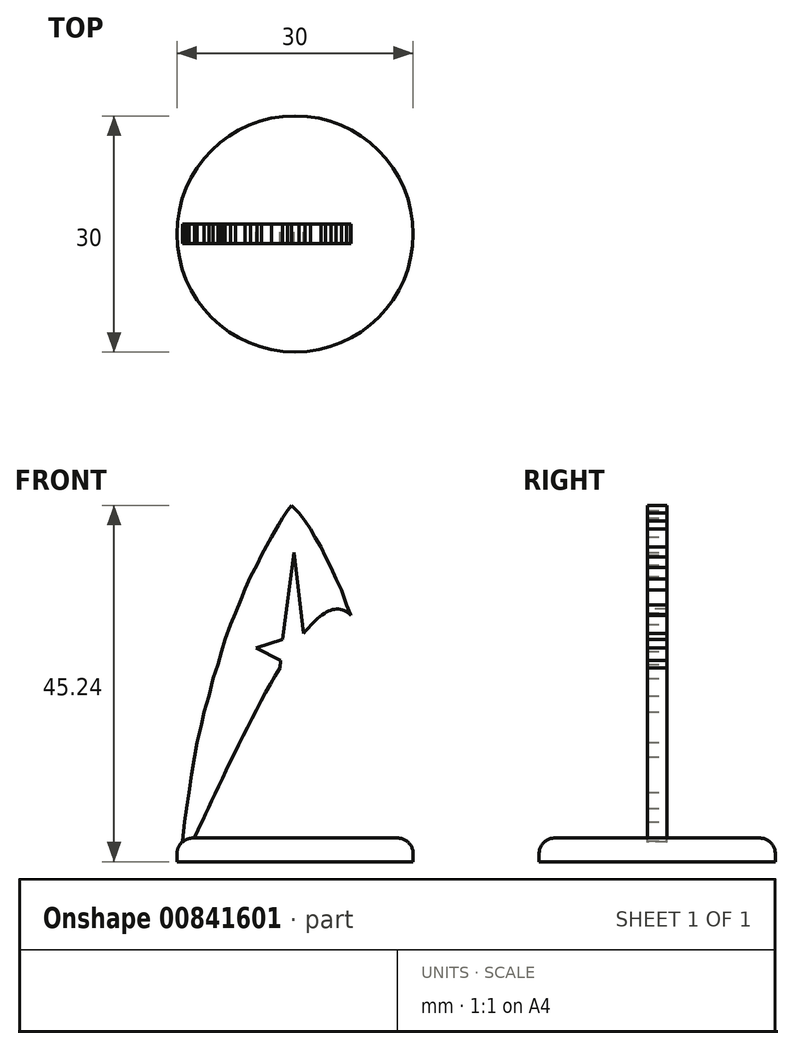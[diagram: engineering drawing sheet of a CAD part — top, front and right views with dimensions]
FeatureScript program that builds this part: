
annotation { "Feature Type Name" : "Feature", "Feature Type Description" : "" }
export const myFeature = defineFeature(function(context is Context, id is Id, definition is map)
    precondition{}
    {
        {
            var Q0;
            Q0=qCreatedBy(makeId("Top.planeOp"),FACE);
            var sketch = newSketch(context, id + "F0", { "sketchPlane" : qUnion([Q0])});
            skCircle(sketch, "E0", {"center": v(0, 0) * mm, "radius": 15 * mm});
            skSolve(sketch);
        }
        {
            var Q0;
            Q0=makeQuery(id+"F0.imprint","IMPRINT",FACE,{"disambiguationData":[TD([[makeQuery(id+"F0.imprint","IMPRINT",EDGE,{"derivedFrom":sQuery(id+"F0.wireOp",EDGE,"E0")}),1.0]])]});
            extrude(context, id + "F1", {"entities" : qUnion([Q0]), "depth" : 3 * mm, "offsetDistance" : 25 * mm});
        }
        {
            var Q0;
            Q0=makeQuery(id+"F1.opExtrude","CAP_EDGE",EDGE,{"disambiguationData":[OSD([sQuery(id+"F0.wireOp",EDGE,"E0")])],"isStart":false});
            fillet(context, id + "F2", {"entities" : qUnion([Q0]), "radius" : 2 * mm, "tangentPropagation" : true, "allowEdgeOverflow" : false});
        }
        {
            var Q0;
            Q0=qCreatedBy(makeId("Front.planeOp"),FACE);
            var sketch = newSketch(context, id + "F3", { "sketchPlane" : qUnion([Q0])});
            skLineSegment(sketch, "E1", {"start": v(-2.26, 21.82) * mm, "end": v(-1.82, 25.53) * mm});
            skLineSegment(sketch, "E2", {"start": v(-1.82, 25.53) * mm, "end": v(-4.93, 27.14) * mm});
            skLineSegment(sketch, "E3", {"start": v(-4.93, 27.14) * mm, "end": v(-1.58, 28.23) * mm});
            skLineSegment(sketch, "E4", {"start": v(-1.58, 28.23) * mm, "end": v(-0.16, 39.29) * mm});
            skLineSegment(sketch, "E5", {"start": v(-0.16, 39.29) * mm, "end": v(1.18, 28.23) * mm});
            skLineSegment(sketch, "E6", {"start": v(1.18, 28.23) * mm, "end": v(4.54, 27.08) * mm});
            skLineSegment(sketch, "E7", {"start": v(4.54, 27.08) * mm, "end": v(1.53, 25.49) * mm});
            skLineSegment(sketch, "E8", {"start": v(1.53, 25.49) * mm, "end": v(1.92, 21.96) * mm});
            skLineSegment(sketch, "E9", {"start": v(1.92, 21.96) * mm, "end": v(-0.11, 25.36) * mm});
            skLineSegment(sketch, "E10", {"start": v(-0.11, 25.36) * mm, "end": v(-2.26, 21.82) * mm});
            skLineSegment(sketch, "E11", {"start": v(-14.46, 0) * mm, "end": v(-14.28, 2.65) * mm});
            skLineSegment(sketch, "E12", {"start": v(-14.28, 2.65) * mm, "end": v(-14.02, 5.03) * mm});
            skLineSegment(sketch, "E13", {"start": v(-14.02, 5.03) * mm, "end": v(-13.75, 6.8) * mm});
            skLineSegment(sketch, "E14", {"start": v(-13.75, 6.8) * mm, "end": v(-13.49, 8.82) * mm});
            skLineSegment(sketch, "E15", {"start": v(-13.49, 8.82) * mm, "end": v(-13.14, 11.11) * mm});
            skLineSegment(sketch, "E16", {"start": v(-13.14, 11.11) * mm, "end": v(-12.78, 13.32) * mm});
            skLineSegment(sketch, "E17", {"start": v(-12.78, 13.32) * mm, "end": v(-12.43, 15.17) * mm});
            skLineSegment(sketch, "E18", {"start": v(-12.43, 15.17) * mm, "end": v(-11.9, 17.46) * mm});
            skLineSegment(sketch, "E19", {"start": v(-11.9, 17.46) * mm, "end": v(-11.55, 19.05) * mm});
            skLineSegment(sketch, "E20", {"start": v(-11.55, 19.05) * mm, "end": v(-10.93, 21.08) * mm});
            skLineSegment(sketch, "E21", {"start": v(-10.93, 21.08) * mm, "end": v(-10.4, 23.28) * mm});
            skLineSegment(sketch, "E22", {"start": v(-10.4, 23.28) * mm, "end": v(-9.78, 25.05) * mm});
            skLineSegment(sketch, "E23", {"start": v(-9.78, 25.05) * mm, "end": v(-9.34, 26.72) * mm});
            skLineSegment(sketch, "E24", {"start": v(-9.34, 26.72) * mm, "end": v(-8.9, 28.22) * mm});
            skLineSegment(sketch, "E25", {"start": v(-8.9, 28.22) * mm, "end": v(-8.2, 30.16) * mm});
            skLineSegment(sketch, "E26", {"start": v(-8.2, 30.16) * mm, "end": v(-7.58, 31.57) * mm});
            skLineSegment(sketch, "E27", {"start": v(-7.58, 31.57) * mm, "end": v(-6.87, 33.34) * mm});
            skLineSegment(sketch, "E28", {"start": v(-6.87, 33.34) * mm, "end": v(-6.34, 34.66) * mm});
            skLineSegment(sketch, "E29", {"start": v(-6.34, 34.66) * mm, "end": v(-5.64, 36.25) * mm});
            skLineSegment(sketch, "E30", {"start": v(-5.64, 36.25) * mm, "end": v(-4.85, 37.66) * mm});
            skLineSegment(sketch, "E31", {"start": v(-4.85, 37.66) * mm, "end": v(-4.23, 38.98) * mm});
            skLineSegment(sketch, "E32", {"start": v(-4.23, 38.98) * mm, "end": v(-3.61, 40.13) * mm});
            skLineSegment(sketch, "E33", {"start": v(-3.61, 40.13) * mm, "end": v(-3, 41.28) * mm});
            skLineSegment(sketch, "E34", {"start": v(-3, 41.28) * mm, "end": v(-2.11, 42.77) * mm});
            skLineSegment(sketch, "E35", {"start": v(-2.11, 42.77) * mm, "end": v(-1.58, 43.66) * mm});
            skLineSegment(sketch, "E36", {"start": v(-1.58, 43.66) * mm, "end": v(-0.96, 44.63) * mm});
            skLineSegment(sketch, "E37", {"start": v(-0.96, 44.63) * mm, "end": v(-0.44, 45.24) * mm});
            skLineSegment(sketch, "E38", {"start": v(-0.44, 45.24) * mm, "end": v(0.53, 44.27) * mm});
            skLineSegment(sketch, "E39", {"start": v(0.53, 44.27) * mm, "end": v(1.24, 43.3) * mm});
            skLineSegment(sketch, "E40", {"start": v(1.24, 43.3) * mm, "end": v(1.95, 42.25) * mm});
            skLineSegment(sketch, "E41", {"start": v(1.95, 42.25) * mm, "end": v(2.56, 41.19) * mm});
            skLineSegment(sketch, "E42", {"start": v(2.56, 41.19) * mm, "end": v(3.27, 39.95) * mm});
            skLineSegment(sketch, "E43", {"start": v(3.27, 39.95) * mm, "end": v(3.89, 38.72) * mm});
            skLineSegment(sketch, "E44", {"start": v(3.89, 38.72) * mm, "end": v(4.6, 37.4) * mm});
            skLineSegment(sketch, "E45", {"start": v(4.6, 37.4) * mm, "end": v(5.2, 35.9) * mm});
            skLineSegment(sketch, "E46", {"start": v(5.2, 35.9) * mm, "end": v(5.91, 34.48) * mm});
            skLineSegment(sketch, "E47", {"start": v(5.91, 34.48) * mm, "end": v(6.53, 32.63) * mm});
            skLineSegment(sketch, "E48", {"start": v(6.53, 32.63) * mm, "end": v(7.06, 31.4) * mm});
            skLineSegment(sketch, "E49", {"start": v(7.06, 31.4) * mm, "end": v(7.5, 30.07) * mm});
            skLineSegment(sketch, "E50", {"start": v(7.5, 30.07) * mm, "end": v(8.2, 28.22) * mm});
            skLineSegment(sketch, "E51", {"start": v(8.2, 28.22) * mm, "end": v(8.82, 26.2) * mm});
            skLineSegment(sketch, "E52", {"start": v(8.82, 26.2) * mm, "end": v(9.53, 23.99) * mm});
            skLineSegment(sketch, "E53", {"start": v(9.53, 23.99) * mm, "end": v(10.15, 21.78) * mm});
            skLineSegment(sketch, "E54", {"start": v(10.15, 21.78) * mm, "end": v(10.68, 19.58) * mm});
            skLineSegment(sketch, "E55", {"start": v(10.68, 19.58) * mm, "end": v(11.3, 17.02) * mm});
            skLineSegment(sketch, "E56", {"start": v(11.3, 17.02) * mm, "end": v(12, 13.67) * mm});
            skLineSegment(sketch, "E57", {"start": v(12, 13.67) * mm, "end": v(12.44, 11.38) * mm});
            skLineSegment(sketch, "E58", {"start": v(12.44, 11.38) * mm, "end": v(12.88, 9.17) * mm});
            skLineSegment(sketch, "E59", {"start": v(12.88, 9.17) * mm, "end": v(13.23, 7.06) * mm});
            skLineSegment(sketch, "E60", {"start": v(13.23, 7.06) * mm, "end": v(13.68, 4.5) * mm});
            skLineSegment(sketch, "E61", {"start": v(13.68, 4.5) * mm, "end": v(12.8, 6.61) * mm});
            skLineSegment(sketch, "E62", {"start": v(12.8, 6.61) * mm, "end": v(12, 8.55) * mm});
            skLineSegment(sketch, "E63", {"start": v(12, 8.55) * mm, "end": v(11.38, 9.88) * mm});
            skLineSegment(sketch, "E64", {"start": v(11.38, 9.88) * mm, "end": v(10.68, 11.02) * mm});
            skLineSegment(sketch, "E65", {"start": v(10.68, 11.02) * mm, "end": v(10.06, 11.9) * mm});
            skLineSegment(sketch, "E66", {"start": v(10.06, 11.9) * mm, "end": v(9.27, 12.88) * mm});
            skLineSegment(sketch, "E67", {"start": v(9.27, 12.88) * mm, "end": v(8.56, 13.76) * mm});
            skLineSegment(sketch, "E68", {"start": v(8.56, 13.76) * mm, "end": v(7.85, 14.64) * mm});
            skLineSegment(sketch, "E69", {"start": v(7.85, 14.64) * mm, "end": v(6.7, 15.43) * mm});
            skLineSegment(sketch, "E70", {"start": v(6.7, 15.43) * mm, "end": v(5.91, 15.88) * mm});
            skLineSegment(sketch, "E71", {"start": v(5.91, 15.88) * mm, "end": v(4.24, 16.32) * mm});
            skLineSegment(sketch, "E72", {"start": v(4.24, 16.32) * mm, "end": v(3, 16.32) * mm});
            skLineSegment(sketch, "E73", {"start": v(3, 16.32) * mm, "end": v(2.12, 16.23) * mm});
            skLineSegment(sketch, "E74", {"start": v(2.12, 16.23) * mm, "end": v(0.98, 15.96) * mm});
            skLineSegment(sketch, "E75", {"start": v(0.98, 15.96) * mm, "end": v(-0.08, 15.61) * mm});
            skLineSegment(sketch, "E76", {"start": v(-0.08, 15.61) * mm, "end": v(-1.14, 15.17) * mm});
            skLineSegment(sketch, "E77", {"start": v(-1.14, 15.17) * mm, "end": v(-1.93, 14.73) * mm});
            skLineSegment(sketch, "E78", {"start": v(-1.93, 14.73) * mm, "end": v(-2.9, 14.11) * mm});
            skLineSegment(sketch, "E79", {"start": v(-2.9, 14.11) * mm, "end": v(-3.7, 13.67) * mm});
            skLineSegment(sketch, "E80", {"start": v(-3.7, 13.67) * mm, "end": v(-4.4, 12.96) * mm});
            skLineSegment(sketch, "E81", {"start": v(-4.4, 12.96) * mm, "end": v(-5.2, 12.44) * mm});
            skLineSegment(sketch, "E82", {"start": v(-5.2, 12.44) * mm, "end": v(-6, 11.64) * mm});
            skLineSegment(sketch, "E83", {"start": v(-6, 11.64) * mm, "end": v(-6.7, 10.94) * mm});
            skLineSegment(sketch, "E84", {"start": v(-6.7, 10.94) * mm, "end": v(-7.5, 9.97) * mm});
            skLineSegment(sketch, "E85", {"start": v(-7.5, 9.97) * mm, "end": v(-8.46, 8.9) * mm});
            skLineSegment(sketch, "E86", {"start": v(-8.46, 8.9) * mm, "end": v(-9.17, 8.03) * mm});
            skLineSegment(sketch, "E87", {"start": v(-9.17, 8.03) * mm, "end": v(-10.4, 6.53) * mm});
            skLineSegment(sketch, "E88", {"start": v(-10.4, 6.53) * mm, "end": v(-11.55, 4.94) * mm});
            skLineSegment(sketch, "E89", {"start": v(-11.55, 4.94) * mm, "end": v(-12.6, 3.17) * mm});
            skLineSegment(sketch, "E90", {"start": v(-12.6, 3.17) * mm, "end": v(-13.49, 1.85) * mm});
            skLineSegment(sketch, "E91", {"start": v(-13.49, 1.85) * mm, "end": v(-14.46, 0) * mm});
            skFitSpline(sketch, "E92", {"points": [v(-14.4, 0.32) * mm, v(-14.4, 0.32) * mm, v(-14.4, 0.32) * mm, v(-14.39, 0.66) * mm, v(-13.21, 26.7) * mm, v(-0.4, 45.32) * mm, v(-0.4, 45.32) * mm, v(-0.4, 45.32) * mm, v(1.88, 43.25) * mm, v(4.79, 37.05) * mm]});
            skFitSpline(sketch, "E93", {"points": [v(4.79, 37.05) * mm, v(7.7, 30.85) * mm, v(11.24, 20.52) * mm, v(13.75, 4) * mm]});
            skFitSpline(sketch, "E94", {"points": [v(13.75, 4) * mm, v(4.7, 32) * mm, v(-11.97, 4.76) * mm, v(-14.4, 0.32) * mm]});
            skSolve(sketch);
        }
        {
            var Q0;
            Q0=makeQuery(id+"F3.imprint","IMPRINT",FACE,{"disambiguationData":[TD([[makeQuery(id+"F3.imprint","IMPRINT",EDGE,{"derivedFrom":sQuery(id+"F3.wireOp",EDGE,"E1")}),1.0]])]});
            extrude(context, id + "F4", {"entities" : qUnion([Q0]), "operationType" : NewBodyOperationType.ADD, "endBound" : BoundingType.SYMMETRIC, "depth" : 2.5 * mm, "offsetDistance" : 25 * mm});
        }
    });
